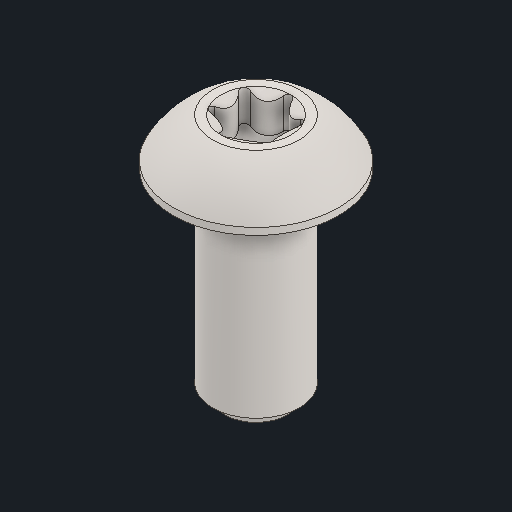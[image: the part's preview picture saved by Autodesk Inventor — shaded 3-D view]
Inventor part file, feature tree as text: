
AUTODESK INVENTOR PART (.ipt)
format: ipt  version: 2024 (Build 280153000, 153)  size: 181,760 bytes
history: native  units: in
note: dims shown in document units (in); Inventor stores cm internally (conversion verified against a paired STEP export)
features: chamfer x1
ambient origin geometry x8: Origin, YZ Plane, XZ Plane, XY Plane, X Axis, Y Axis, Z Axis, Center Point
bodies: Solid1 (feature_tree)
feature tree (1):
  chamfer  "Chamfer2"  [1 undecoded]
note: 1 required parameter value undecoded (feature->parameter linkage not recoverable at this tier; creation-order binding heuristic only, values carry confidence <= 0.55)
